# Revit family: 304_c137c99ddd6c48c68c43dd0c54ba50
name_source: partatom
category: Pipe Accessories
units: mm (PartAtom-declared; Revit-internal decimal feet)

## family parameters
Always vertical = Yes
Cut with Voids When Loaded = No
Part Type = Valve - Breaks Into
Round Connector Dimension = Use Diameter
Shared = No
Work Plane-Based = No

## types (15) — shared parameters
CAT0 = Yes
Description = Automatic balancing valve
H1 = 118 mm  [stored 0.387139 ft]
H1__ve = -118 mm  [stored -0.387139 ft]
L = 170 mm  [stored 0.557743 ft]
L1 = 49 mm  [stored 0.160761 ft]
L2D = 170 mm  [stored 0.557743 ft]
L2D_Min = 3048 mm  [stored 10 ft]
LL = 85 mm  [stored 0.278871 ft]
Manufacturer = Frese A/S
QmdConnectorList = 301;D;302;D
URL = https://www.frese.eu
W2D = 100 mm  [stored 0.328084 ft]
magiPartTypeId = 304
magiProductFamilyId = c137c99ddd6c48c68c43dd0c54ba50

## per-type parameters (varying)
| type | D | DC | DC2 | magiProductId |
| Frese ALPHA DN100 PN25 | 100 mm | 163 mm  [stored 0.534777 ft] | 82 mm | 498321085e1544c0838e9e7040ff8f |
| Frese ALPHA DN125 PN25 | 125 mm | 193 mm  [stored 0.633202 ft] | 97 mm | 448ebd9ee870445d95944e13e76e9d |
| Frese ALPHA DN150 PN25 | 150 mm | 216 mm  [stored 0.708661 ft] | 108 mm  [stored 0.354331 ft] | 526e012f13544c7188f3f4d78a8c13 |
| Frese ALPHA DN200 PN25 | 200 mm | 271 mm  [stored 0.889108 ft] | 136 mm | da351d5b1a7c4d39972231e9e7571e |
| Frese ALPHA DN250 PN25 | 200 mm | 271 mm  [stored 0.889108 ft] | 136 mm | b16843e0869f4f5a818c32dfade59e |
| Frese ALPHA DN300 PN25 | 315 mm | 383 mm  [stored 1.25656 ft] | 192 mm | 041015fe805b4611854f194ad169cc |
| Frese ALPHA DN350 PN25 | 355 mm | 443 mm  [stored 1.45341 ft] | 222 mm | 5a664dc9fc8e48fb89ee781babb4ba |
| Frese ALPHA DN400 PN25 | 405 mm | 496 mm  [stored 1.6273 ft] | 248 mm  [stored 0.813648 ft] | 4c01f070735c4976a15e0e72c5520c |
| Frese ALPHA DN450 PN25 | 455 mm | 545 mm  [stored 1.78806 ft] | 273 mm | 134cbc351daa4a879993f6a7856a29 |
| Frese ALPHA DN50 PN25 | 80 mm | 100 mm  [stored 0.328084 ft] | 50 mm  [stored 0.164042 ft] | 2941daa40ab1446f9b4279ee0a94e0 |
| Frese ALPHA DN500 PN25 | 508 mm | 601 mm  [stored 1.97178 ft] | 301 mm | abfcb19c934d4e969af642ef60540c |
| Frese ALPHA DN600 PN25 | 610 mm | 715 mm  [stored 2.3458 ft] | 358 mm | 3bfa9a8b568b46698f35a2a93e153f |
| Frese ALPHA DN65 PN25 | 80 mm | 119 mm  [stored 0.39042 ft] | 60 mm | 31df510f192340d69b25db3dc50c42 |
| Frese ALPHA DN80 PN25 | 80 mm | 131 mm  [stored 0.42979 ft] | 66 mm  [stored 0.216535 ft] | 694b2aad8b4649669bc8c59a2c534d |
| Frese ALPHA DN800 PN25 | 760 mm | 880 mm  [stored 2.88714 ft] | 440 mm  [stored 1.44357 ft] | 182edc3f71a74e838e562fb7c94ec7 |

note: column(s) folded — value = type name in every type: MC Product Code

note: [stored X ft] marks values corroborated as IEEE doubles in the binary element streams (Revit-internal decimal feet)

## geometry (parser evidence)
native form markers: Sweep x1
no freeform markers — native parametric forms only
